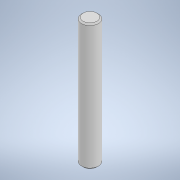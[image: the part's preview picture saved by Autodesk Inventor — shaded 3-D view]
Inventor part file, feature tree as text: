
AUTODESK INVENTOR PART (.ipt)
format: ipt  version: 2020 (Build 240168000, 168)  size: 96,256 bytes
history: native  units: mm
features: extrude x1, chamfer x1, sketch x1
ambient origin geometry x8: Origin, YZ Plane, XZ Plane, XY Plane, X Axis, Y Axis, Z Axis, Center Point
bodies: Solid1 (feature_tree)
feature tree (3):
  extrude  "Extrusion1"  Depth=45.0mm TaperAngle=0.0deg
  chamfer  "Chamfer1"  Distance=0.5mm Angle=45.0deg
  sketch  "Sketch1"  dims[d0=6.0mm d1=45.0mm d2=0.0mm d3=0.5mm d4=2.0mm d5=45.0deg]
